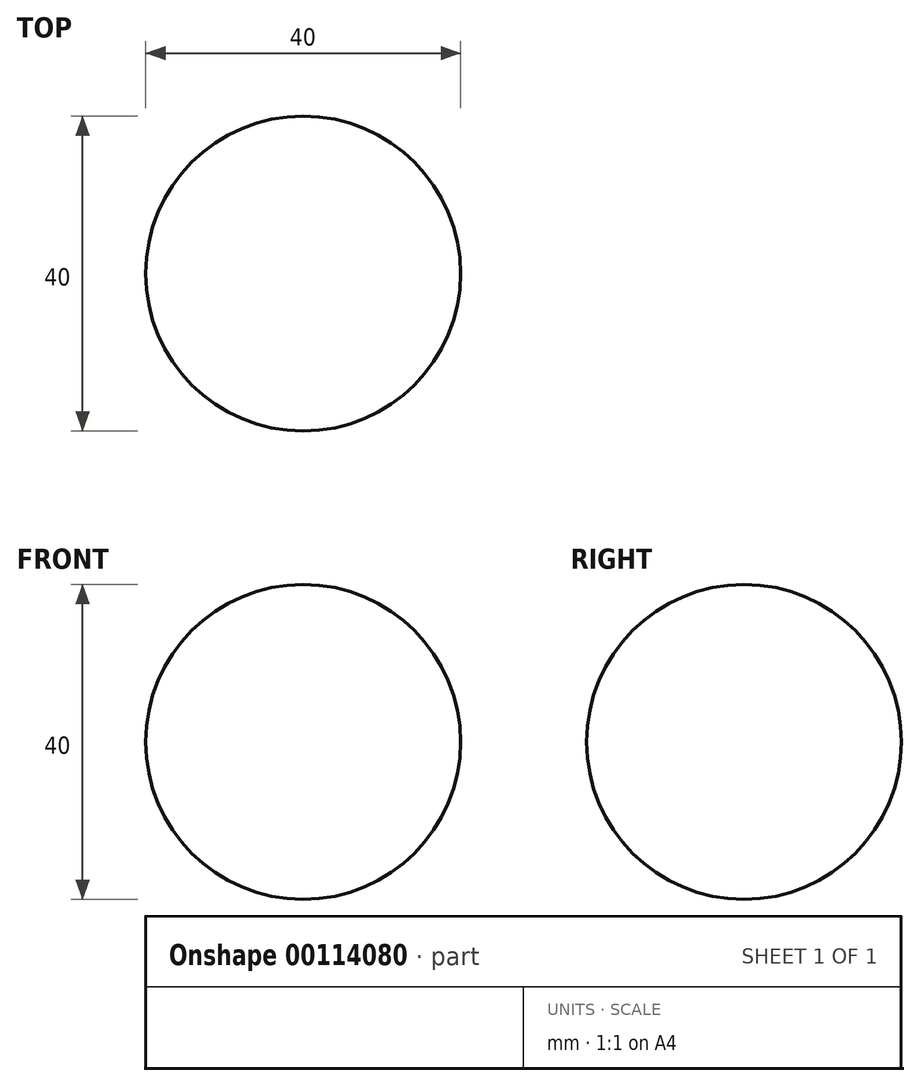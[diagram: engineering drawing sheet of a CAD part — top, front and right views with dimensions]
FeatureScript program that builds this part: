
annotation { "Feature Type Name" : "Feature", "Feature Type Description" : "" }
export const myFeature = defineFeature(function(context is Context, id is Id, definition is map)
    precondition{}
    {
        {
            var Q0;
            Q0=qCreatedBy(makeId("Front.planeOp"),FACE);
            var sketch = newSketch(context, id + "F0", { "sketchPlane" : qUnion([Q0])});
            skCircle(sketch, "E0", {"center": v(0, 0) * mm, "radius": 20 * mm});
            skSolve(sketch);
        }
        {
            var Q0;
            Q0=makeQuery(id+"F0.imprint","IMPRINT",FACE,{"disambiguationData":[TD([[makeQuery(id+"F0.imprint","IMPRINT",EDGE,{"derivedFrom":sQuery(id+"F0.wireOp",EDGE,"E0")}),1.0]])]});
            extrude(context, id + "F1", {"entities" : qUnion([Q0]), "endBound" : BoundingType.SYMMETRIC, "depth" : 40 * mm});
        }
        {
            var Q0;
            Q0=makeQuery(id+"F1.opExtrude","CAP_EDGE",EDGE,{"disambiguationData":[OSD([sQuery(id+"F0.wireOp",EDGE,"E0")])],"isStart":true});
            var Q1;
            Q1=makeQuery(id+"F1.opExtrude","CAP_EDGE",EDGE,{"disambiguationData":[OSD([sQuery(id+"F0.wireOp",EDGE,"E0")])],"isStart":false});
            fillet(context, id + "F2", {"entities" : qUnion([Q0, Q1]), "radius" : 20 * mm, "tangentPropagation" : true, "allowEdgeOverflow" : false});
        }
    });
